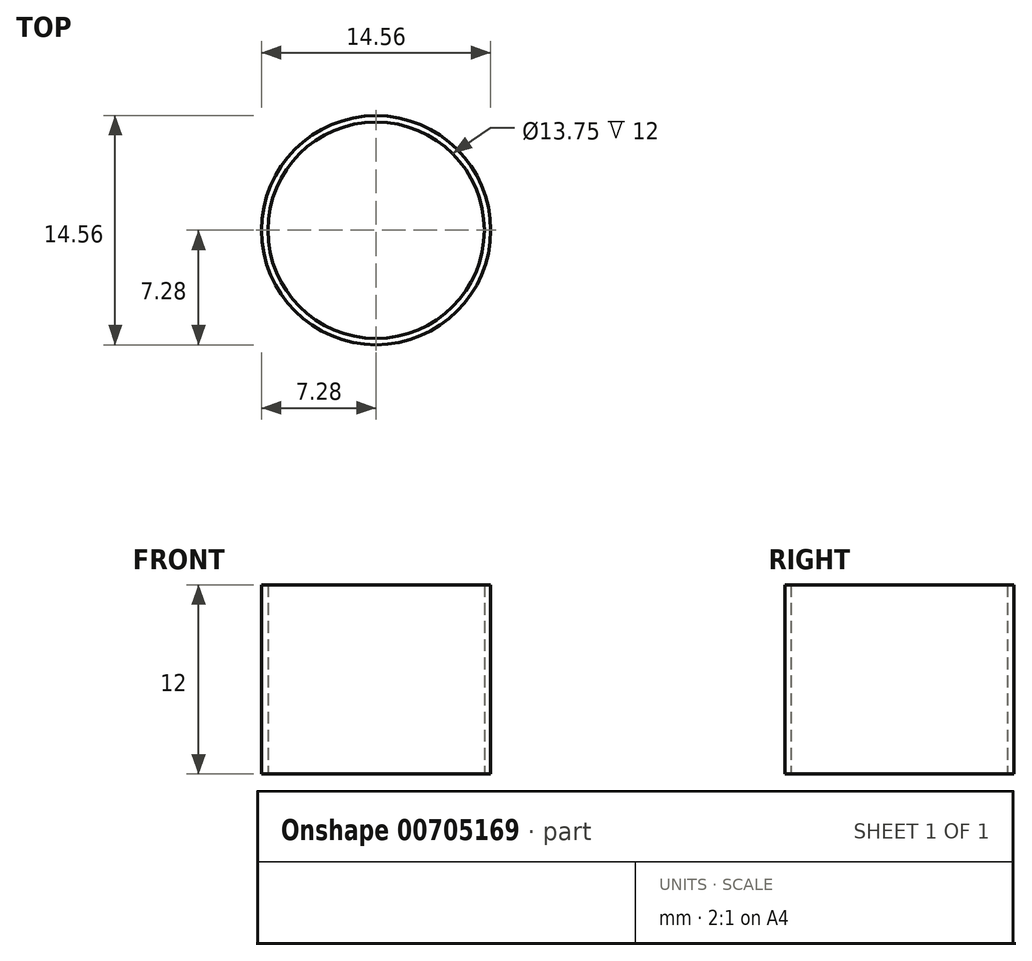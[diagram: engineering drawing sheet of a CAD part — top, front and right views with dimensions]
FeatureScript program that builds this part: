
annotation { "Feature Type Name" : "Feature", "Feature Type Description" : "" }
export const myFeature = defineFeature(function(context is Context, id is Id, definition is map)
    precondition{}
    {
        {
            var Q0;
            Q0=qCreatedBy(makeId("Top.planeOp"),FACE);
            var sketch = newSketch(context, id + "F0", { "sketchPlane" : qUnion([Q0])});
            skCircle(sketch, "E0", {"center": v(0, 0) * mm, "radius": 7.28 * mm});
            skCircle(sketch, "E1", {"center": v(0, 0) * mm, "radius": 6.88 * mm});
            skSolve(sketch);
        }
        {
            var Q0;
            Q0=makeQuery(id+"F0.imprint","IMPRINT",FACE,{"disambiguationData":[TD([[makeQuery(id+"F0.imprint","IMPRINT",EDGE,{"derivedFrom":sQuery(id+"F0.wireOp",EDGE,"E0")}),1.0]])]});
            extrude(context, id + "F1", {"entities" : qUnion([Q0]), "depth" : 12 * mm, "offsetDistance" : 25 * mm});
        }
    });
